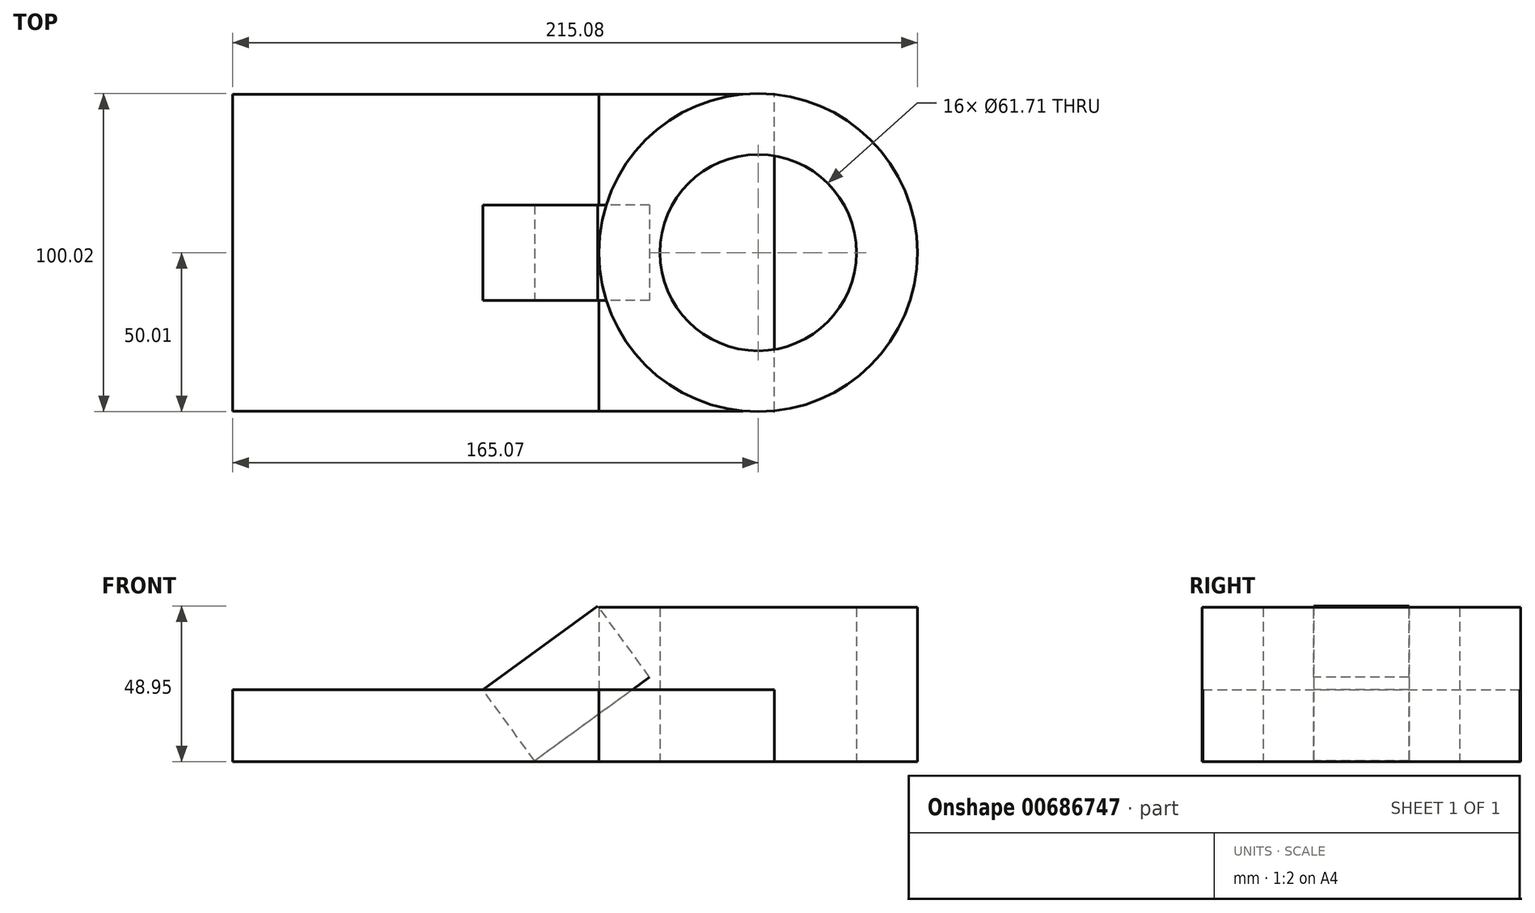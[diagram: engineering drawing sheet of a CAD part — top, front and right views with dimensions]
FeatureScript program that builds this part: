
annotation { "Feature Type Name" : "Feature", "Feature Type Description" : "" }
export const myFeature = defineFeature(function(context is Context, id is Id, definition is map)
    precondition{}
    {
        {
            var Q0;
            Q0=qCreatedBy(makeId("Top.planeOp"),FACE);
            var sketch = newSketch(context, id + "F0", { "sketchPlane" : qUnion([Q0])});
            skCircle(sketch, "E0", {"center": v(0, 0) * mm, "radius": 30.85 * mm});
            skCircle(sketch, "E1", {"center": v(0, 0) * mm, "radius": 50.01 * mm});
            skSolve(sketch);
        }
        {
            var Q0;
            Q0=makeQuery(id+"F0.imprint","IMPRINT",FACE,{"disambiguationData":[TD([[makeQuery(id+"F0.imprint","IMPRINT",EDGE,{"derivedFrom":sQuery(id+"F0.wireOp",EDGE,"E0")}),-1.0]])]});
            extrude(context, id + "F1", {"entities" : qUnion([Q0]), "depth" : 48.5 * mm, "offsetDistance" : 25.4 * mm});
        }
        {
            var Q0;
            Q0=qCreatedBy(makeId("Front.planeOp"),FACE);
            var sketch = newSketch(context, id + "F2", { "sketchPlane" : qUnion([Q0])});
            skLineSegment(sketch, "E2.bottom", {"start": v(-50.03, 0) * mm, "end": v(-165.07, 0) * mm});
            skLineSegment(sketch, "E2.top", {"start": v(-50.03, 22.64) * mm, "end": v(-165.07, 22.64) * mm});
            skLineSegment(sketch, "E2.left", {"start": v(-50.03, 0) * mm, "end": v(-50.03, 22.64) * mm});
            skLineSegment(sketch, "E2.right", {"start": v(-165.07, 0) * mm, "end": v(-165.07, 22.64) * mm});
            skSolve(sketch);
        }
        {
            var Q0;
            Q0=makeQuery(id+"F2.imprint","IMPRINT",FACE,{"disambiguationData":[TD([[makeQuery(id+"F2.imprint","IMPRINT",EDGE,{"derivedFrom":sQuery(id+"F2.wireOp",EDGE,"E2.bottom")}),-1.0]])]});
            extrude(context, id + "F3", {"entities" : qUnion([Q0]), "endBound" : BoundingType.SYMMETRIC, "depth" : 99.57 * mm, "offsetDistance" : 25.4 * mm});
        }
        {
            var Q0;
            Q0=makeQuery(id+"F3.opExtrude","SWEPT_FACE",FACE,{"disambiguationData":[OSD([sQuery(id+"F2.wireOp",EDGE,"E2.left")])]});
            extrude(context, id + "F4", {"entities" : qUnion([Q0]), "depth" : 55.12 * mm, "offsetDistance" : 25.4 * mm});
        }
        {
            var Q0;
            Q0=qCreatedBy(makeId("Front.planeOp"),FACE);
            var sketch = newSketch(context, id + "F5", { "sketchPlane" : qUnion([Q0])});
            skLineSegment(sketch, "E3", {"start": v(-50.4, 48.95) * mm, "end": v(-86.5, 22.64) * mm});
            skSolve(sketch);
        }
        {
            var Q0;
            Q0=sQuery(id+"F5.wireOp",EDGE,"E3");
            extrude(context, id + "F6", {"bodyType" : ToolBodyType.SURFACE, "surfaceEntities" : qUnion([Q0]), "endBound" : BoundingType.SYMMETRIC, "depth" : 29.97 * mm, "offsetDistance" : 25.4 * mm});
        }
        {
            var Q0;
            Q0=makeQuery(id+"F6.opExtrude","SWEPT_FACE",FACE,{"disambiguationData":[OSD([sQuery(id+"F5.wireOp",EDGE,"E3")])]});
            extrude(context, id + "F7", {"entities" : qUnion([Q0]), "oppositeDirection" : true, "depth" : 27.7 * mm, "offsetDistance" : 25.4 * mm});
        }
    });
